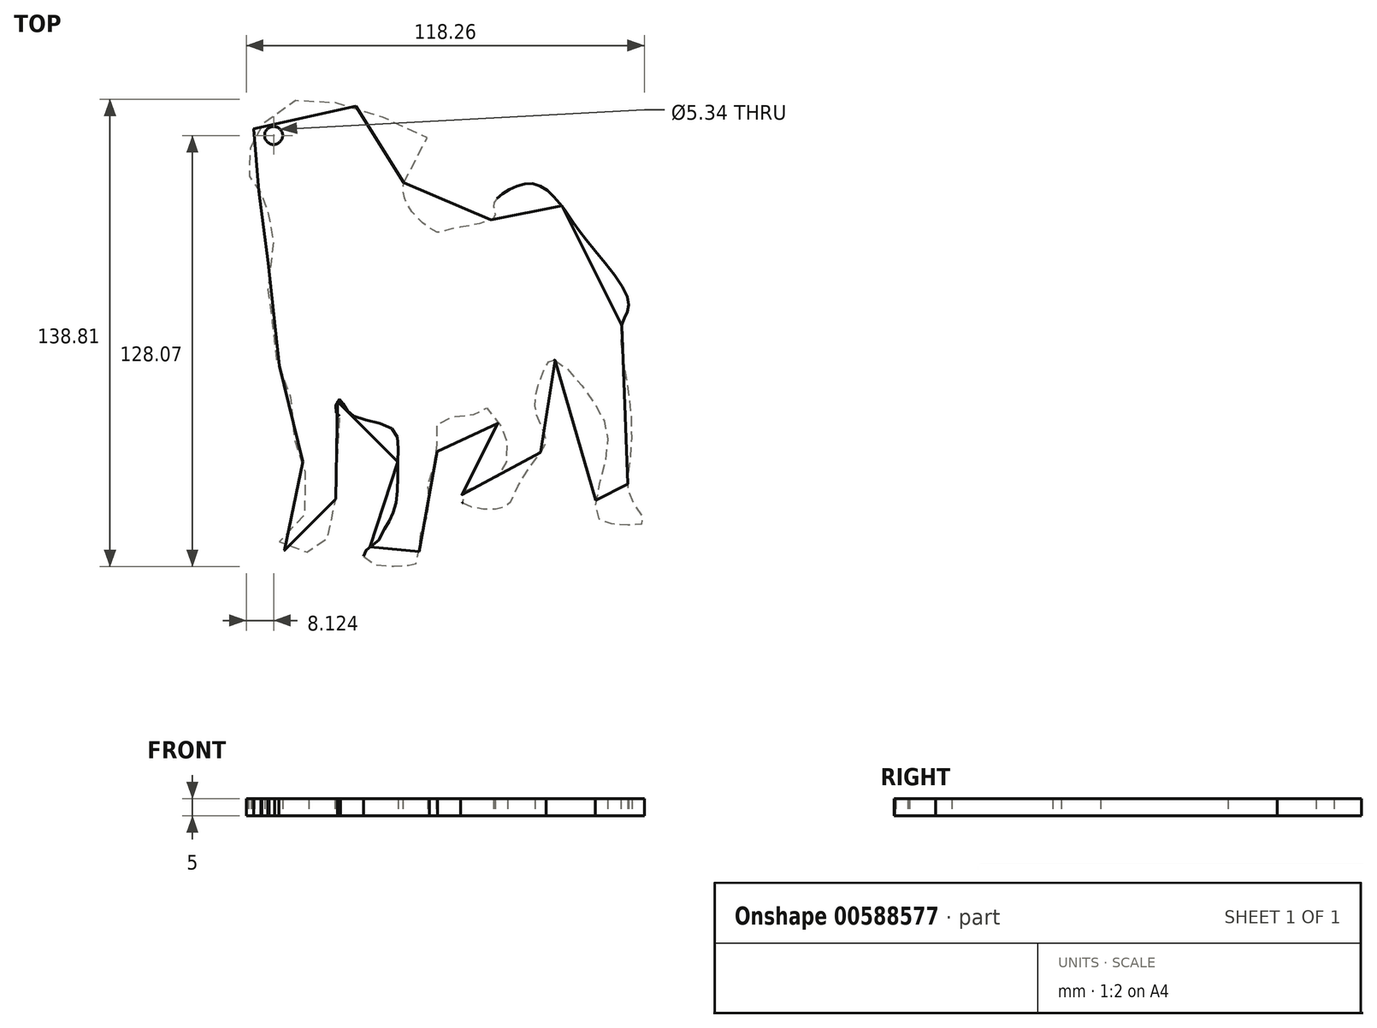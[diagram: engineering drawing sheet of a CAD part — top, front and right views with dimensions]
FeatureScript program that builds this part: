
annotation { "Feature Type Name" : "Feature", "Feature Type Description" : "" }
export const myFeature = defineFeature(function(context is Context, id is Id, definition is map)
    precondition{}
    {
        {
            var Q0;
            Q0=qCreatedBy(makeId("Top.planeOp"),FACE);
            var sketch = newSketch(context, id + "F0", { "sketchPlane" : qUnion([Q0])});
            skFitSpline(sketch, "E0", {"points": [v(-25.07, 42.2) * mm, v(-17.93, 54.86) * mm, v(-27.7, 60.03) * mm, v(-37.68, 64.51) * mm, v(-52.25, 66.65) * mm, v(-57.14, 66.63) * mm, v(-62.16, 62.28) * mm, v(-70.2, 57.8) * mm, v(-71.12, 54.84) * mm, v(-70.66, 48.71) * mm, v(-71.8, 44.78) * mm, v(-69.46, 42.9) * mm, v(-69.62, 40.52) * mm, v(-67.54, 39.26) * mm, v(-67.56, 35.28) * mm, v(-66.15, 33.88) * mm, v(-64, 30.32) * mm, v(-63.47, 26.5) * mm, v(-65.14, 19.85) * mm, v(-64.7, 5.4) * mm, v(-63.75, 2.07) * mm, v(-65, -1.58) * mm, v(-62.92, -10.27) * mm, v(-59.64, -17.34) * mm, v(-58.06, -28.48) * mm, v(-57.4, -34.8) * mm, v(-56.37, -36.8) * mm, v(-53.78, -47.37) * mm, v(-54.32, -55.93) * mm, v(-60.4, -62.89) * mm, v(-62.17, -64.93) * mm, v(-59.17, -67.55) * mm, v(-50.83, -67.26) * mm, v(-48.72, -67) * mm, v(-47.22, -59.65) * mm, v(-45.72, -53.53) * mm, v(-44.78, -46.58) * mm, v(-44.67, -36.32) * mm, v(-44.27, -26.78) * mm, v(-45.48, -25.57) * mm, v(-44.25, -22.17) * mm, v(-42.79, -24.02) * mm, v(-39.5, -27.37) * mm, v(-28.38, -31.02) * mm, v(-26.81, -39.33) * mm, v(-27.25, -51.88) * mm, v(-29.34, -58.06) * mm, v(-31.67, -62.1) * mm, v(-32.45, -63.83) * mm, v(-35.9, -66.58) * mm, v(-36.96, -69.19) * mm, v(-30.65, -71.8) * mm, v(-24.1, -71.33) * mm, v(-22.03, -71.6) * mm, v(-20.58, -67.52) * mm, v(-19.91, -61.45) * mm, v(-17.55, -54.4) * mm, v(-17.94, -47.82) * mm, v(-15.15, -37.52) * mm, v(-14.63, -28.6) * mm, v(-4.16, -26.55) * mm, v(0, -24.8) * mm, v(2.54, -28.88) * mm, v(4.46, -30.96) * mm, v(5.55, -39.77) * mm, v(2.02, -45.7) * mm, v(-5.96, -48.75) * mm, v(-7.97, -52.5) * mm, v(4.45, -54.17) * mm, v(8.38, -48.8) * mm, v(15.24, -38.26) * mm, v(17.12, -33.71) * mm, v(14, -25.33) * mm, v(16.03, -14.7) * mm, v(19.32, -10.48) * mm, v(30.68, -22.02) * mm, v(35.38, -36.42) * mm, v(32.01, -56.43) * mm, v(39.01, -59.26) * mm, v(46.32, -58.47) * mm, v(42.23, -51.27) * mm, v(42.1, -41) * mm, v(41.92, -21.1) * mm, v(39.65, 0) * mm, v(41.66, 6.9) * mm, v(27.77, 26.9) * mm, v(21.93, 35.19) * mm, v(14.24, 41.72) * mm, v(6.08, 40.08) * mm, v(1.54, 35.55) * mm, v(1.72, 31.92) * mm, v(-12.42, 28.11) * mm, v(-14.42, 27.39) * mm, v(-20.04, 30.83) * mm, v(-25.07, 42.2) * mm]});
            skCircle(sketch, "E1", {"center": v(-63.78, 56.25) * mm, "radius": 2.67 * mm});
            skSolve(sketch);
        }
        {
            var Q0;
            Q0=makeQuery(id+"F0.imprint","IMPRINT",FACE,{"disambiguationData":[TD([[makeQuery(id+"F0.imprint","IMPRINT",EDGE,{"derivedFrom":sQuery(id+"F0.wireOp",EDGE,"E0")}),1.0]])]});
            extrude(context, id + "F1", {"entities" : qUnion([Q0]), "depth" : 5 * mm, "offsetDistance" : 25 * mm});
        }
        {
            var Q0;
            Q0=qCreatedBy(makeId("Top.planeOp"),FACE);
            var sketch = newSketch(context, id + "F2", { "sketchPlane" : qUnion([Q0])});
            skCircle(sketch, "E2", {"center": v(-62.26, 52.86) * mm, "radius": 2.74 * mm});
            skSolve(sketch);
        }
        {
            var Q0;
            Q0=makeQuery(id+"F1.opExtrude","CAP_FACE",FACE,{"disambiguationData":[OSD([sQuery(id+"F0.wireOp",EDGE,"E0")])],"isStart":false});
            extrude(context, id + "F3", {"entities" : qUnion([Q0]), "operationType" : NewBodyOperationType.ADD, "oppositeDirection" : true, "depth" : 5 * mm, "offsetDistance" : 25 * mm});
        }
        {
            var Q0;
            Q0=sQuery(id+"F2.wireOp",EDGE,"E2");
            extrude(context, id + "F4", {"bodyType" : ToolBodyType.SURFACE, "operationType" : NewBodyOperationType.REMOVE, "surfaceEntities" : qUnion([Q0]), "oppositeDirection" : true, "depth" : 25 * mm, "offsetDistance" : 25 * mm});
        }
    });
